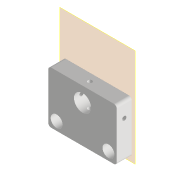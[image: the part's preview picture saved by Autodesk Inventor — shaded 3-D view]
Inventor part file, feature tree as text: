
AUTODESK INVENTOR PART (.ipt)
format: ipt  version: 2022 (Build 260153000, 153)  size: 141,312 bytes
history: native  units: mm
features: extrude x3, sketch x3, other x2, plane x1, reference x1
ambient origin geometry x8: Origin, YZ Plane, XZ Plane, XY Plane, X Axis, Y Axis, Z Axis, Center Point
bodies: Volumenkörper1 (feature_tree)
feature tree (10):
  plane  "Arbeitsebene1"
  extrude  "Extrusion1"  Depth=8.0mm
  extrude  "Extrusion2"  Depth=25.0mm
  extrude  "Extrusion3"  TaperAngle=0.0deg  [1 undecoded]
  sketch  "Skizze1"  dims[d0=8.0mm d1=8.0mm]
  reference  "Referenz1"
  sketch  "Skizze2"  dims[d2=11.5mm d3=25.0mm]
  sketch  "Skizze3"  dims[d4=35.0mm d5=0.0mm d6=2.0mm d7=10.0mm d8=0.0mm d9=2.8mm d10=5.75mm d11=0.0mm d12=0.0mm d13=2.8mm d14=0.0mm d15=0.0mm]
  other  "Anglerfish_lunchbox_m12large_flipped_v0.iam"
  other  "Anglerfish_coverslipclamp_top:1"
note: 1 required parameter value undecoded (feature->parameter linkage not recoverable at this tier; creation-order binding heuristic only, values carry confidence <= 0.55)
